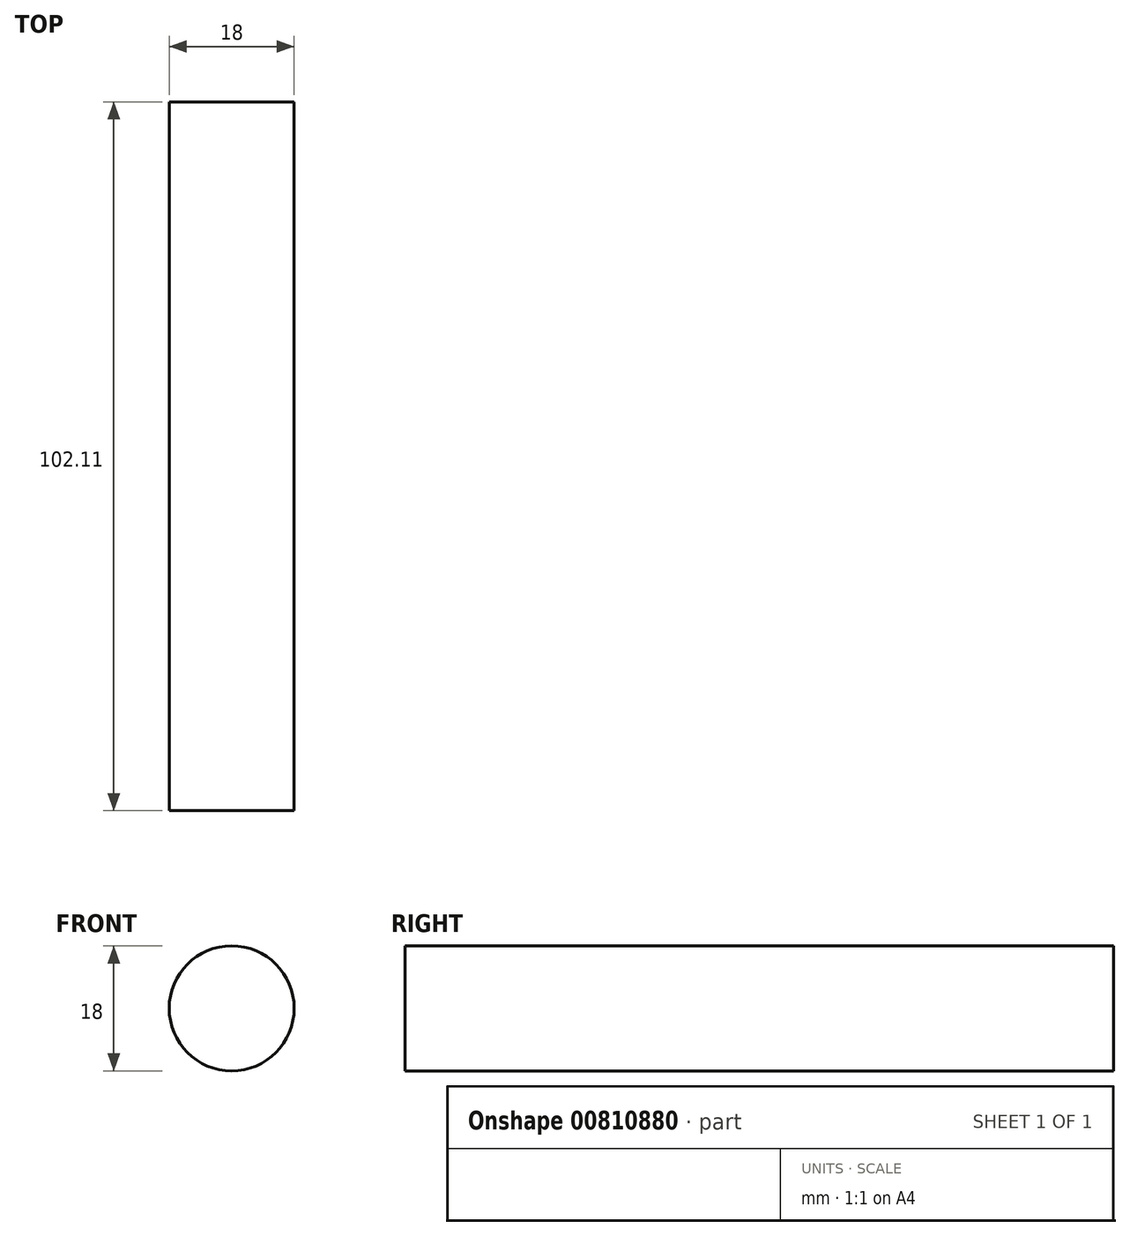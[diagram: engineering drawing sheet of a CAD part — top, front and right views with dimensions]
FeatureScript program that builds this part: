
annotation { "Feature Type Name" : "Feature", "Feature Type Description" : "" }
export const myFeature = defineFeature(function(context is Context, id is Id, definition is map)
    precondition{}
    {
        {
            var Q0;
            Q0=qCreatedBy(makeId("Front.planeOp"),FACE);
            var sketch = newSketch(context, id + "F0", { "sketchPlane" : qUnion([Q0])});
            skCircle(sketch, "E0", {"center": v(0, 0) * mm, "radius": 9 * mm});
            skSolve(sketch);
        }
        {
            var Q0;
            Q0 = qSketchRegion(id + "F0", true);
            extrude(context, id + "F1", {"entities" : qUnion([Q0]), "depth" : 102.1 * mm, "offsetDistance" : 25.4 * mm});
        }
    });
